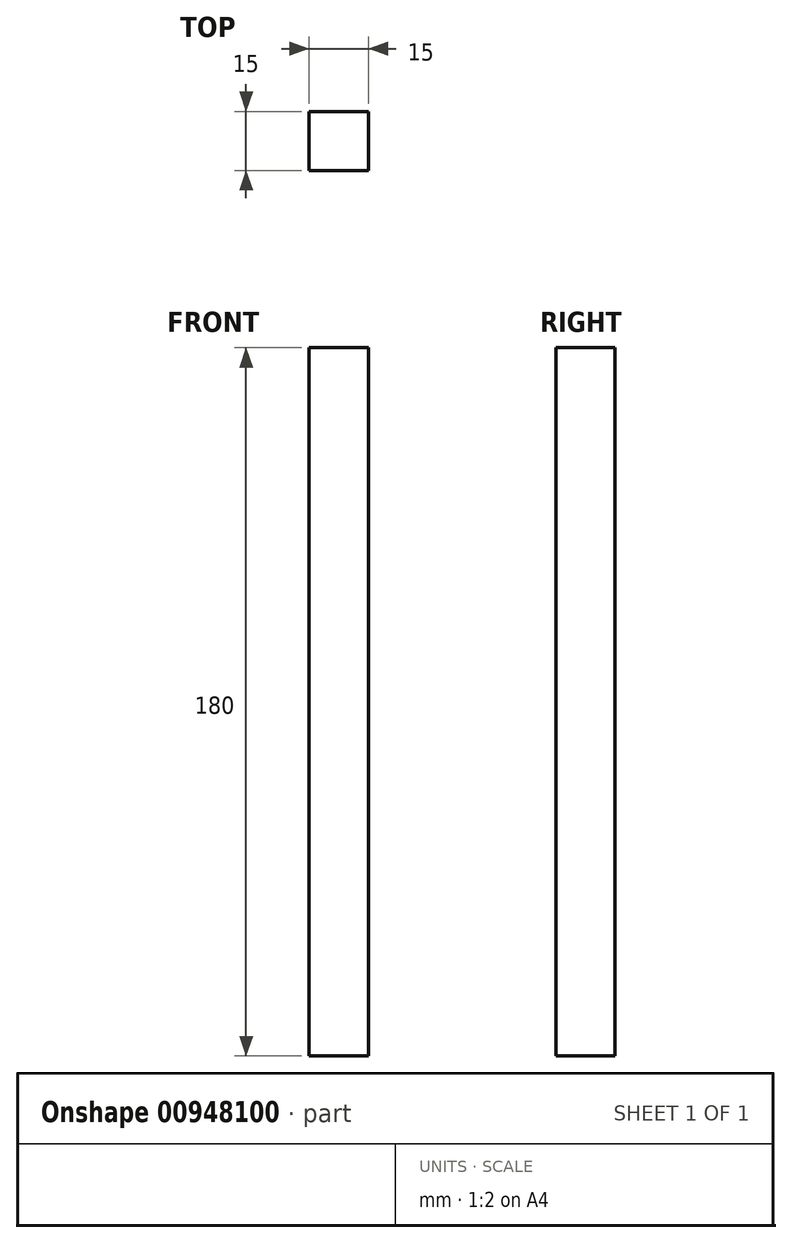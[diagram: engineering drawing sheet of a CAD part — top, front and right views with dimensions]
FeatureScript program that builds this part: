
annotation { "Feature Type Name" : "Feature", "Feature Type Description" : "" }
export const myFeature = defineFeature(function(context is Context, id is Id, definition is map)
    precondition{}
    {
        {
            var Q0;
            Q0=qCreatedBy(makeId("Top.planeOp"),FACE);
            var sketch = newSketch(context, id + "F0", { "sketchPlane" : qUnion([Q0])});
            skLineSegment(sketch, "E0.bottom", {"start": v(-7.5, 7.5) * mm, "end": v(7.5, 7.5) * mm});
            skLineSegment(sketch, "E0.top", {"start": v(-7.5, -7.5) * mm, "end": v(7.5, -7.5) * mm});
            skLineSegment(sketch, "E0.left", {"start": v(-7.5, 7.5) * mm, "end": v(-7.5, -7.5) * mm});
            skLineSegment(sketch, "E0.right", {"start": v(7.5, 7.5) * mm, "end": v(7.5, -7.5) * mm});
            skPoint(sketch, "E0.middle", {"position": v(0, 0) * mm});
            skSolve(sketch);
        }
        {
            var Q0;
            Q0=makeQuery(id+"F0.imprint","IMPRINT",FACE,{"disambiguationData":[TD([[makeQuery(id+"F0.imprint","IMPRINT",EDGE,{"derivedFrom":sQuery(id+"F0.wireOp",EDGE,"E0.bottom")}),-1.0]])]});
            extrude(context, id + "F1", {"entities" : qUnion([Q0]), "depth" : 180 * mm, "offsetDistance" : 25 * mm});
        }
    });
